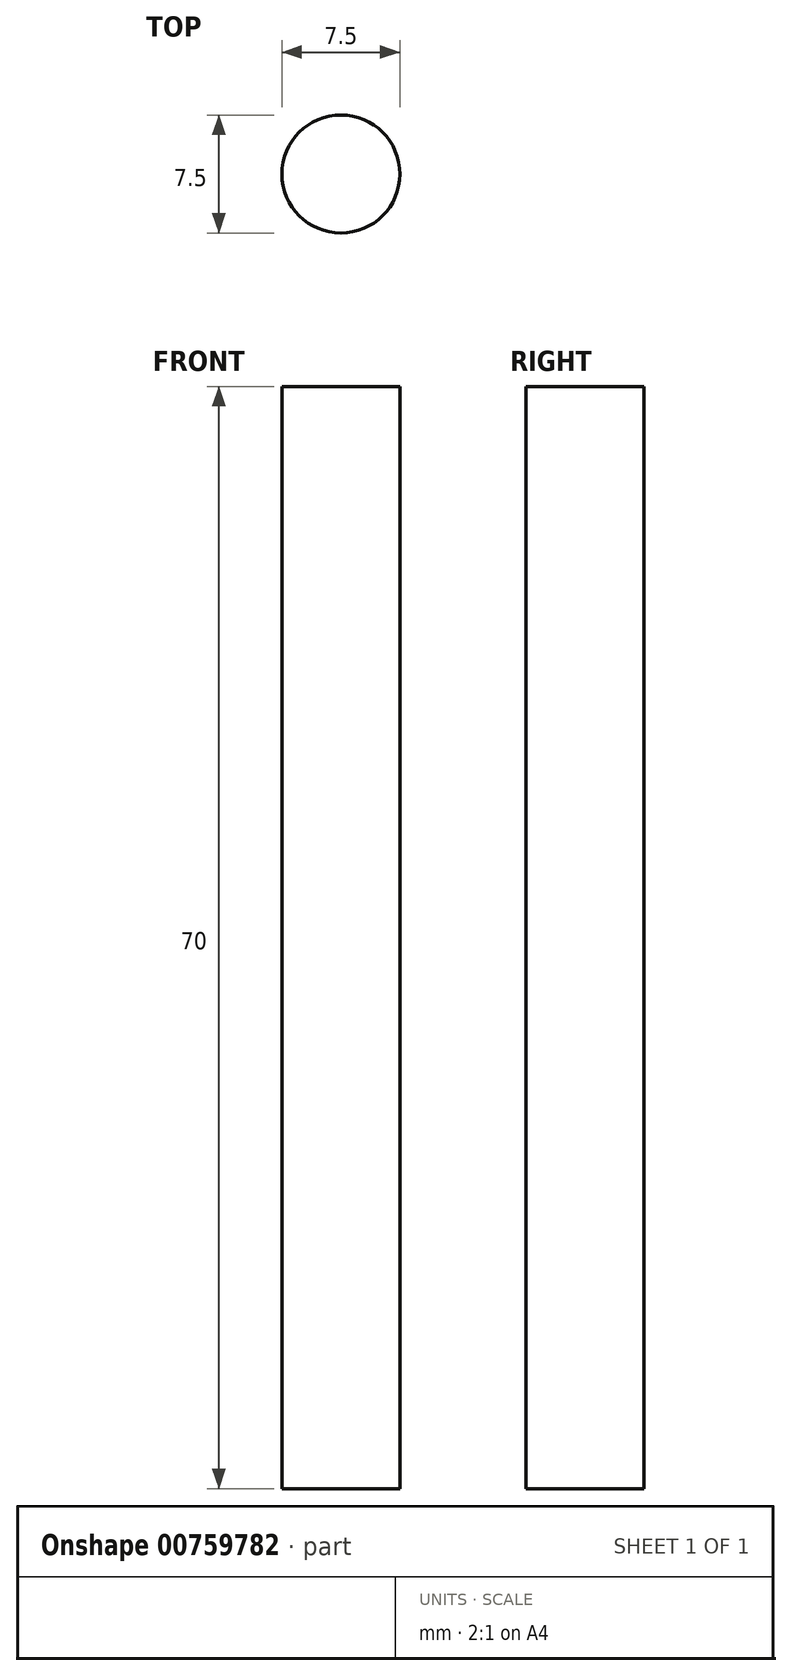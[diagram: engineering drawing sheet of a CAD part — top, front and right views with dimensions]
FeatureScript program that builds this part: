
annotation { "Feature Type Name" : "Feature", "Feature Type Description" : "" }
export const myFeature = defineFeature(function(context is Context, id is Id, definition is map)
    precondition{}
    {
        {
            var Q0;
            Q0=qCreatedBy(makeId("Front.planeOp"),FACE);
            var sketch = newSketch(context, id + "F0", { "sketchPlane" : qUnion([Q0])});
            skLineSegment(sketch, "E0.bottom", {"start": v(0, 0) * mm, "end": v(-3.75, 0) * mm});
            skLineSegment(sketch, "E0.top", {"start": v(0, 70) * mm, "end": v(-3.75, 70) * mm});
            skLineSegment(sketch, "E0.left", {"start": v(0, 0) * mm, "end": v(0, 70) * mm});
            skLineSegment(sketch, "E0.right", {"start": v(-3.75, 0) * mm, "end": v(-3.75, 70) * mm});
            skSolve(sketch);
        }
        {
            var Q0;
            Q0=makeQuery(id+"F0.imprint","IMPRINT",FACE,{"disambiguationData":[TD([[makeQuery(id+"F0.imprint","IMPRINT",EDGE,{"derivedFrom":sQuery(id+"F0.wireOp",EDGE,"E0.bottom")}),-1.0]])]});
            var Q1;
            Q1=sQuery(id+"F0.wireOp",EDGE,"E0.left");
            revolve(context, id + "F1", {"surfaceOperationType" : NewSurfaceOperationType.NEW, "entities" : qUnion([Q0]), "axis" : qUnion([Q1]), "revolveType" : RevolveType.FULL});
        }
    });
